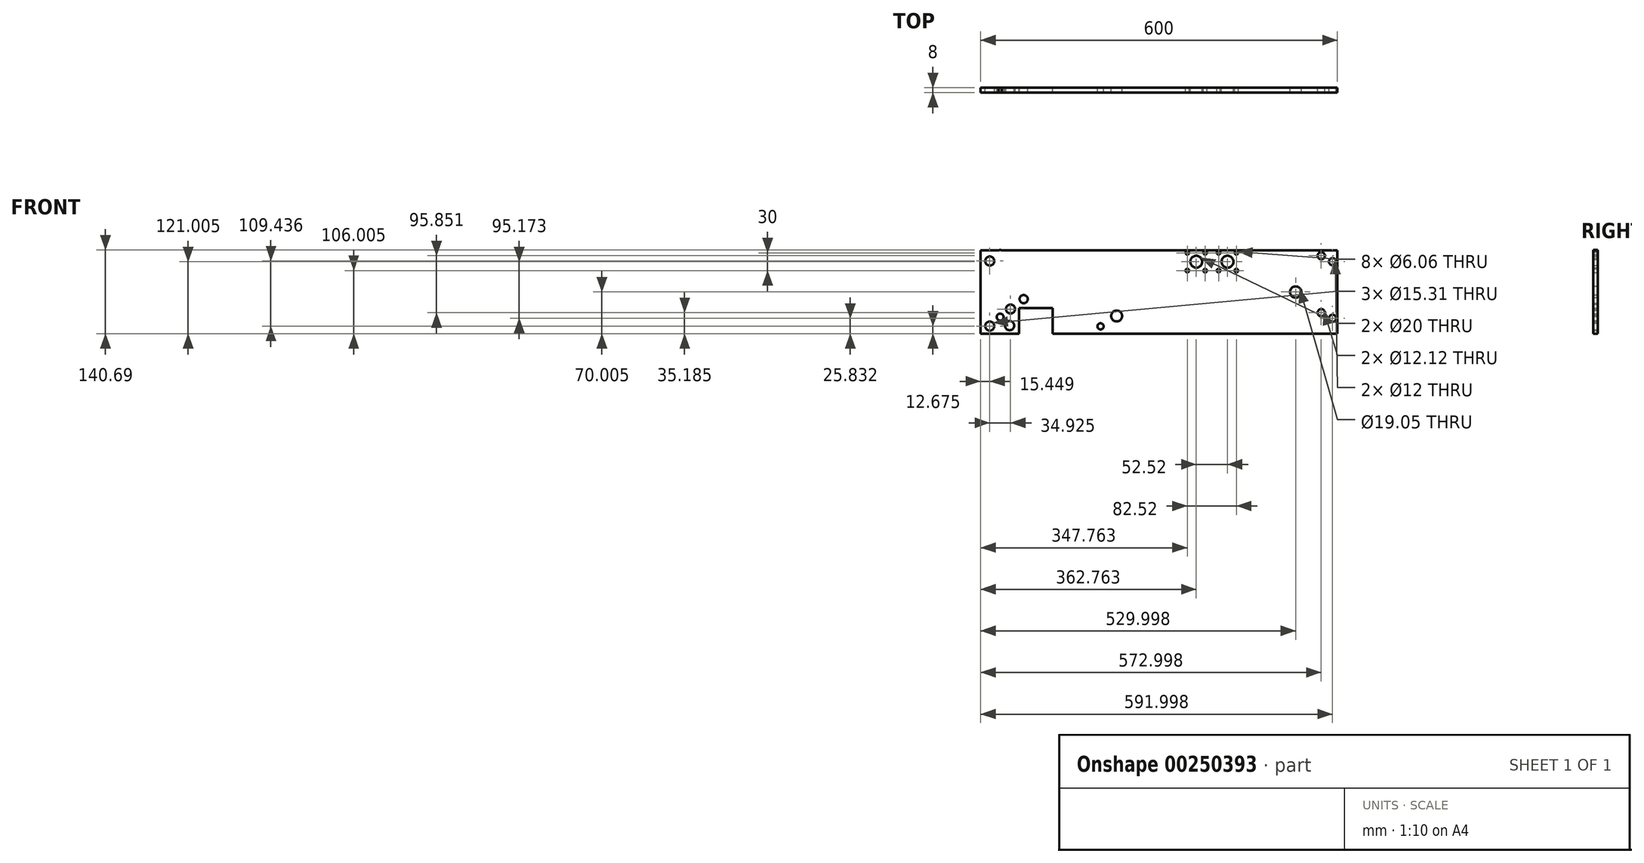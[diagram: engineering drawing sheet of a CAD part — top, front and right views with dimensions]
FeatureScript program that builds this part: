
annotation { "Feature Type Name" : "Feature", "Feature Type Description" : "" }
export const myFeature = defineFeature(function(context is Context, id is Id, definition is map)
    precondition{}
    {
        {
            var Q0;
            Q0=qCreatedBy(makeId("Front.planeOp"),FACE);
            var sketch = newSketch(context, id + "F0", { "sketchPlane" : qUnion([Q0])});
            skLineSegment(sketch, "E0.bottom", {"start": v(500.75, 119.12) * mm, "end": v(-99.25, 119.12) * mm});
            skLineSegment(sketch, "E0.top", {"start": v(500.75, -20.88) * mm, "end": v(21.75, -20.88) * mm});
            skLineSegment(sketch, "E0.left", {"start": v(500.75, 119.12) * mm, "end": v(500.75, -20.88) * mm});
            skLineSegment(sketch, "E0.right", {"start": v(-99.25, 119.12) * mm, "end": v(-99.25, -20.88) * mm});
            skLineSegment(sketch, "E1", {"start": v(-34.25, -20.88) * mm, "end": v(-34.25, 22.12) * mm});
            skLineSegment(sketch, "E2", {"start": v(-34.25, 22.12) * mm, "end": v(21.75, 22.12) * mm});
            skLineSegment(sketch, "E3", {"start": v(21.75, 22.12) * mm, "end": v(21.75, -20.88) * mm});
            skLineSegment(sketch, "E4.trimOffspring", {"start": v(-34.25, -20.88) * mm, "end": v(-99.25, -20.88) * mm});
            skCircle(sketch, "E5", {"center": v(-83.8, -8.2) * mm, "radius": 7.65 * mm});
            skCircle(sketch, "E6", {"center": v(-66.34, 6.98) * mm, "radius": 5.77 * mm});
            skCircle(sketch, "E7", {"center": v(-50.43, -7.43) * mm, "radius": 7.76 * mm});
            skCircle(sketch, "E8", {"center": v(-48.88, 20.51) * mm, "radius": 7.65 * mm});
            skCircle(sketch, "E9", {"center": v(-26.76, 37.2) * mm, "radius": 6.9 * mm});
            skCircle(sketch, "E10", {"center": v(-83.8, 101.23) * mm, "radius": 7.65 * mm});
            skCircle(sketch, "E11", {"center": v(-66.34, 114.04) * mm, "radius": 5.77 * mm});
            skCircle(sketch, "E12", {"center": v(102.47, -8.6) * mm, "radius": 5.2 * mm});
            skCircle(sketch, "E13", {"center": v(129.63, 8.87) * mm, "radius": 9.16 * mm});
            skCircle(sketch, "E14", {"center": v(263.51, 100.12) * mm, "radius": 10 * mm});
            skCircle(sketch, "E15", {"center": v(316.03, 100.12) * mm, "radius": 10 * mm});
            skCircle(sketch, "E16", {"center": v(248.51, 115.12) * mm, "radius": 3.03 * mm});
            skCircle(sketch, "E17", {"center": v(248.51, 85.12) * mm, "radius": 3.03 * mm});
            skCircle(sketch, "E18", {"center": v(278.51, 115.12) * mm, "radius": 3.03 * mm});
            skCircle(sketch, "E19", {"center": v(278.51, 85.12) * mm, "radius": 3.03 * mm});
            skCircle(sketch, "E20", {"center": v(473.75, 110.16) * mm, "radius": 6.06 * mm});
            skCircle(sketch, "E21", {"center": v(492.75, 100.12) * mm, "radius": 6 * mm});
            skCircle(sketch, "E22", {"center": v(473.75, 14.3) * mm, "radius": 6.06 * mm});
            skCircle(sketch, "E23", {"center": v(492.75, 4.95) * mm, "radius": 6 * mm});
            skCircle(sketch, "E24", {"center": v(301.03, 115.12) * mm, "radius": 3.03 * mm});
            skCircle(sketch, "E25", {"center": v(301.03, 85.12) * mm, "radius": 3.03 * mm});
            skCircle(sketch, "E26", {"center": v(331.03, 115.12) * mm, "radius": 3.03 * mm});
            skCircle(sketch, "E27", {"center": v(331.03, 85.12) * mm, "radius": 3.03 * mm});
            skCircle(sketch, "E28", {"center": v(430.75, 49.12) * mm, "radius": 9.52 * mm});
            skSolve(sketch);
        }
        {
            var Q0;
            Q0 = qSketchRegion(id + "F0", true);
            extrude(context, id + "F1", {"entities" : qUnion([Q0]), "depth" : 8 * mm});
        }
    });
